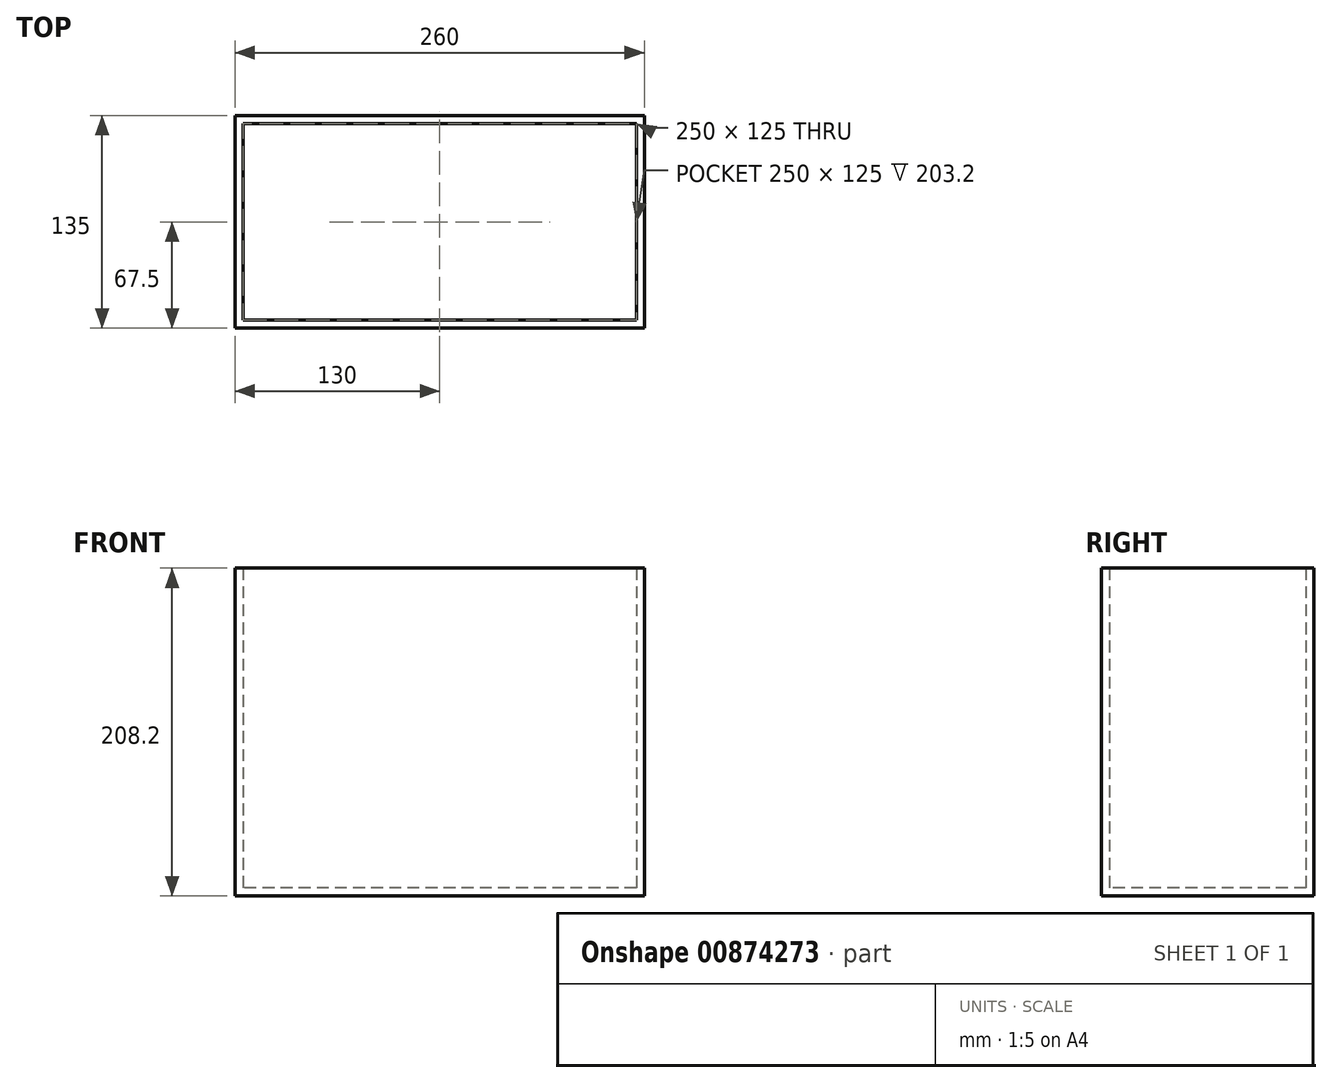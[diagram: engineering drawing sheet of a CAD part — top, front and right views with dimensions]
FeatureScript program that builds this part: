
annotation { "Feature Type Name" : "Feature", "Feature Type Description" : "" }
export const myFeature = defineFeature(function(context is Context, id is Id, definition is map)
    precondition{}
    {
        {
            var Q0;
            Q0=qCreatedBy(makeId("Top.planeOp"),FACE);
            var sketch = newSketch(context, id + "F0", { "sketchPlane" : qUnion([Q0])});
            skLineSegment(sketch, "E0.bottom", {"start": v(125, 62.5) * mm, "end": v(-125, 62.5) * mm});
            skLineSegment(sketch, "E0.top", {"start": v(125, -62.5) * mm, "end": v(-125, -62.5) * mm});
            skLineSegment(sketch, "E0.left", {"start": v(125, 62.5) * mm, "end": v(125, -62.5) * mm});
            skLineSegment(sketch, "E0.right", {"start": v(-125, 62.5) * mm, "end": v(-125, -62.5) * mm});
            skPoint(sketch, "E0.middle", {"position": v(0, 0) * mm});
            skSolve(sketch);
        }
        {
            var Q0;
            Q0 = qSketchRegion(id + "F0", true);
            var Q1;
            Q1=makeQuery(id+"F0.imprint","IMPRINT",FACE,{"disambiguationData":[TD([[makeQuery(id+"F0.imprint","IMPRINT",EDGE,{"derivedFrom":sQuery(id+"F0.wireOp",EDGE,"E0.bottom")}),1.0]])]});
            extrude(context, id + "F1", {"entities" : qUnion([Q0, Q1]), "depth" : 203.2 * mm, "offsetDistance" : 25 * mm});
        }
        {
            var Q0;
            Q0=makeQuery(id+"F1.opExtrude","CAP_FACE",FACE,{"disambiguationData":[OSD([sQuery(id+"F0.wireOp",EDGE,"E0.bottom"),sQuery(id+"F0.wireOp",EDGE,"E0.top"),sQuery(id+"F0.wireOp",EDGE,"E0.left"),sQuery(id+"F0.wireOp",EDGE,"E0.right")])],"isStart":false});
            shell(context, id + "F2", {"entities" : qUnion([Q0]), "thickness" : 5 * mm, "oppositeDirection" : true});
        }
    });
